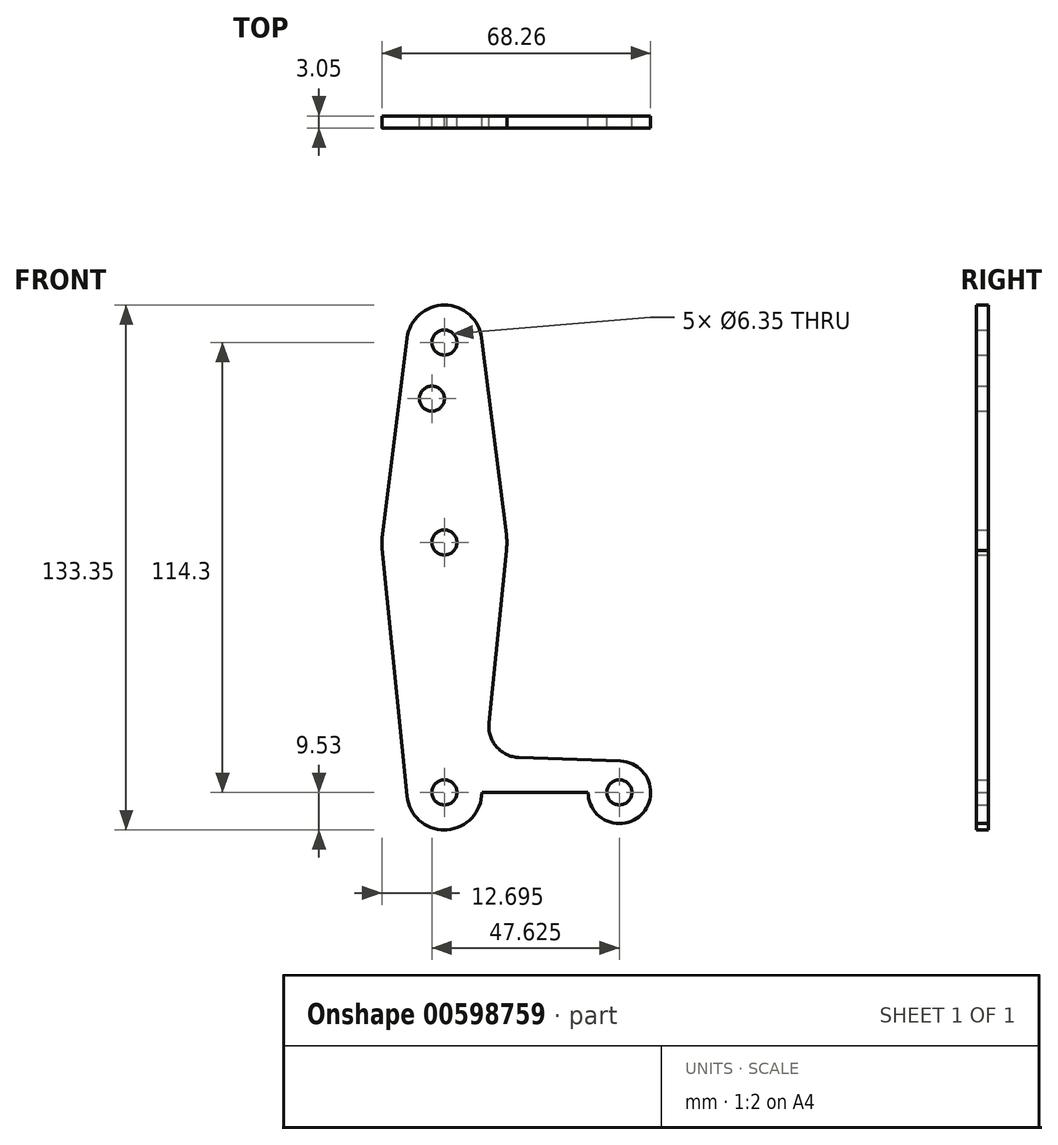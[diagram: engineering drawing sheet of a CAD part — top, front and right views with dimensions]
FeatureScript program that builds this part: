
annotation { "Feature Type Name" : "Feature", "Feature Type Description" : "" }
export const myFeature = defineFeature(function(context is Context, id is Id, definition is map)
    precondition{}
    {
        {
            var Q0;
            Q0=qCreatedBy(makeId("Front.planeOp"),FACE);
            var sketch = newSketch(context, id + "F0", { "sketchPlane" : qUnion([Q0])});
            skCircle(sketch, "E0", {"center": v(0, 0) * mm, "radius": 15.88 * mm});
            skCircle(sketch, "E1", {"center": v(0, 50.8) * mm, "radius": 9.53 * mm});
            skCircle(sketch, "E2", {"center": v(0, -63.5) * mm, "radius": 9.53 * mm});
            skCircle(sketch, "E3", {"center": v(44.45, -63.5) * mm, "radius": 7.94 * mm});
            skLineSegment(sketch, "E4", {"start": v(0, 50.8) * mm, "end": v(0, 0) * mm});
            skLineSegment(sketch, "E5", {"start": v(0, -63.5) * mm, "end": v(0, 0) * mm});
            skLineSegment(sketch, "E6", {"start": v(0, -63.5) * mm, "end": v(44.45, -63.5) * mm});
            skLineSegment(sketch, "E7", {"start": v(-9.46, 51.91) * mm, "end": v(-15.75, 1.98) * mm});
            skLineSegment(sketch, "E8", {"start": v(-15.8, -1.59) * mm, "end": v(-9.48, -64.45) * mm});
            skLineSegment(sketch, "E9", {"start": v(18.97, -54.65) * mm, "end": v(44.73, -55.57) * mm});
            skLineSegment(sketch, "E10", {"start": v(0, -73.03) * mm, "end": v(44.73, -71.43) * mm});
            skLineSegment(sketch, "E11", {"start": v(9.46, 51.91) * mm, "end": v(15.75, 1.98) * mm});
            skLineSegment(sketch, "E12", {"start": v(15.75, -1.98) * mm, "end": v(11.34, -45.91) * mm});
            skCircle(sketch, "E13", {"center": v(0, 50.8) * mm, "radius": 3.18 * mm});
            skCircle(sketch, "E14", {"center": v(0, 0) * mm, "radius": 3.18 * mm});
            skCircle(sketch, "E15", {"center": v(0, -63.5) * mm, "radius": 3.18 * mm});
            skCircle(sketch, "E16", {"center": v(44.45, -63.5) * mm, "radius": 3.18 * mm});
            skArc(sketch, "E17.filletArc", {"start": v(11.34, -45.91) * mm, "mid": v(13.26, -51.93) * mm, "end": v(18.97, -54.65) * mm});
            skCircle(sketch, "E18", {"center": v(-3.17, 36.53) * mm, "radius": 3.18 * mm});
            skSolve(sketch);
        }
        {
            var Q0;
            {var subQ0=sQuery(id+"F0.wireOp",EDGE,"E5");var subQ1=sQuery(id+"F0.wireOp",EDGE,"E2");var subQ2=makeQuery(id+"F0.imprint","INTERSECT",VERTEX,{"derivedFrom":[subQ1,subQ0]});Q0=makeQuery(id+"F0.imprint","IMPRINT",FACE,{"disambiguationData":[TD([[makeQuery(id+"F0.imprint","IMPRINT",EDGE,{"disambiguationData":[TD([[subQ2,1.0]])],"derivedFrom":subQ1}),1.0]])]});}
            var Q1;
            {var subQ5=sQuery(id+"F0.wireOp",EDGE,"E9");Q1=makeQuery(id+"F0.imprint","IMPRINT",FACE,{"disambiguationData":[TD([[makeQuery(id+"F0.imprint","IMPRINT",EDGE,{"derivedFrom":subQ5}),-1.0]])]});}
            var Q2;
            {var subQ0=sQuery(id+"F0.wireOp",EDGE,"E10");var subQ1=sQuery(id+"F0.wireOp",EDGE,"E2");var subQ2=makeQuery(id+"F0.imprint","INTERSECT",VERTEX,{"disambiguationData":[OD(1.0)],"derivedFrom":[subQ1,subQ0]});Q2=makeQuery(id+"F0.imprint","IMPRINT",FACE,{"disambiguationData":[TD([[makeQuery(id+"F0.imprint","IMPRINT",EDGE,{"disambiguationData":[TD([[subQ2,-1.0]])],"derivedFrom":subQ1}),-1.0]])]});}
            var Q3;
            {var subQ1=sQuery(id+"F0.wireOp",EDGE,"E2");var subQ5=makeQuery(id+"F0.imprint","INTERSECT",VERTEX,{"derivedFrom":[subQ1,sQuery(id+"F0.wireOp",EDGE,"E8")]});Q3=makeQuery(id+"F0.imprint","IMPRINT",FACE,{"disambiguationData":[TD([[makeQuery(id+"F0.imprint","IMPRINT",EDGE,{"disambiguationData":[TD([[subQ5,1.0]])],"derivedFrom":subQ1}),1.0]])]});}
            var Q4;
            Q4=makeQuery(id+"F0.imprint","IMPRINT",FACE,{"disambiguationData":[TD([[makeQuery(id+"F0.imprint","IMPRINT",EDGE,{"derivedFrom":sQuery(id+"F0.wireOp",EDGE,"E16")}),-1.0]])]});
            var Q5;
            {var subQ0=sQuery(id+"F0.wireOp",EDGE,"E8");Q5=makeQuery(id+"F0.imprint","IMPRINT",FACE,{"disambiguationData":[TD([[makeQuery(id+"F0.imprint","IMPRINT",EDGE,{"derivedFrom":subQ0}),1.0]])]});}
            var Q6;
            {var subQ1=sQuery(id+"F0.wireOp",EDGE,"E0");var subQ8=makeQuery(id+"F0.imprint","INTERSECT",VERTEX,{"derivedFrom":[subQ1,sQuery(id+"F0.wireOp",EDGE,"E7")]});Q6=makeQuery(id+"F0.imprint","IMPRINT",FACE,{"disambiguationData":[TD([[makeQuery(id+"F0.imprint","IMPRINT",EDGE,{"disambiguationData":[TD([[subQ8,1.0]])],"derivedFrom":subQ1}),1.0]])]});}
            var Q7;
            {var subQ1=sQuery(id+"F0.wireOp",EDGE,"E0");var subQ8=makeQuery(id+"F0.imprint","INTERSECT",VERTEX,{"derivedFrom":[subQ1,sQuery(id+"F0.wireOp",EDGE,"E11")]});Q7=makeQuery(id+"F0.imprint","IMPRINT",FACE,{"disambiguationData":[TD([[makeQuery(id+"F0.imprint","IMPRINT",EDGE,{"disambiguationData":[TD([[subQ8,-1.0]])],"derivedFrom":subQ1}),1.0]])]});}
            var Q8;
            {var subQ6=sQuery(id+"F0.wireOp",EDGE,"E11");Q8=makeQuery(id+"F0.imprint","IMPRINT",FACE,{"disambiguationData":[TD([[makeQuery(id+"F0.imprint","IMPRINT",EDGE,{"derivedFrom":subQ6}),-1.0]])]});}
            var Q9;
            {var subQ5=sQuery(id+"F0.wireOp",EDGE,"E7");Q9=makeQuery(id+"F0.imprint","IMPRINT",FACE,{"disambiguationData":[TD([[makeQuery(id+"F0.imprint","IMPRINT",EDGE,{"derivedFrom":subQ5}),1.0]])]});}
            var Q10;
            Q10=makeQuery(id+"F0.imprint","IMPRINT",FACE,{"disambiguationData":[TD([[makeQuery(id+"F0.imprint","IMPRINT",EDGE,{"derivedFrom":sQuery(id+"F0.wireOp",EDGE,"E13")}),-1.0]])]});
            extrude(context, id + "F1", {"entities" : qUnion([Q0, Q1, Q2, Q3, Q4, Q5, Q6, Q7, Q8, Q9, Q10]), "depth" : 3.05 * mm, "offsetDistance" : 25.4 * mm});
        }
    });
